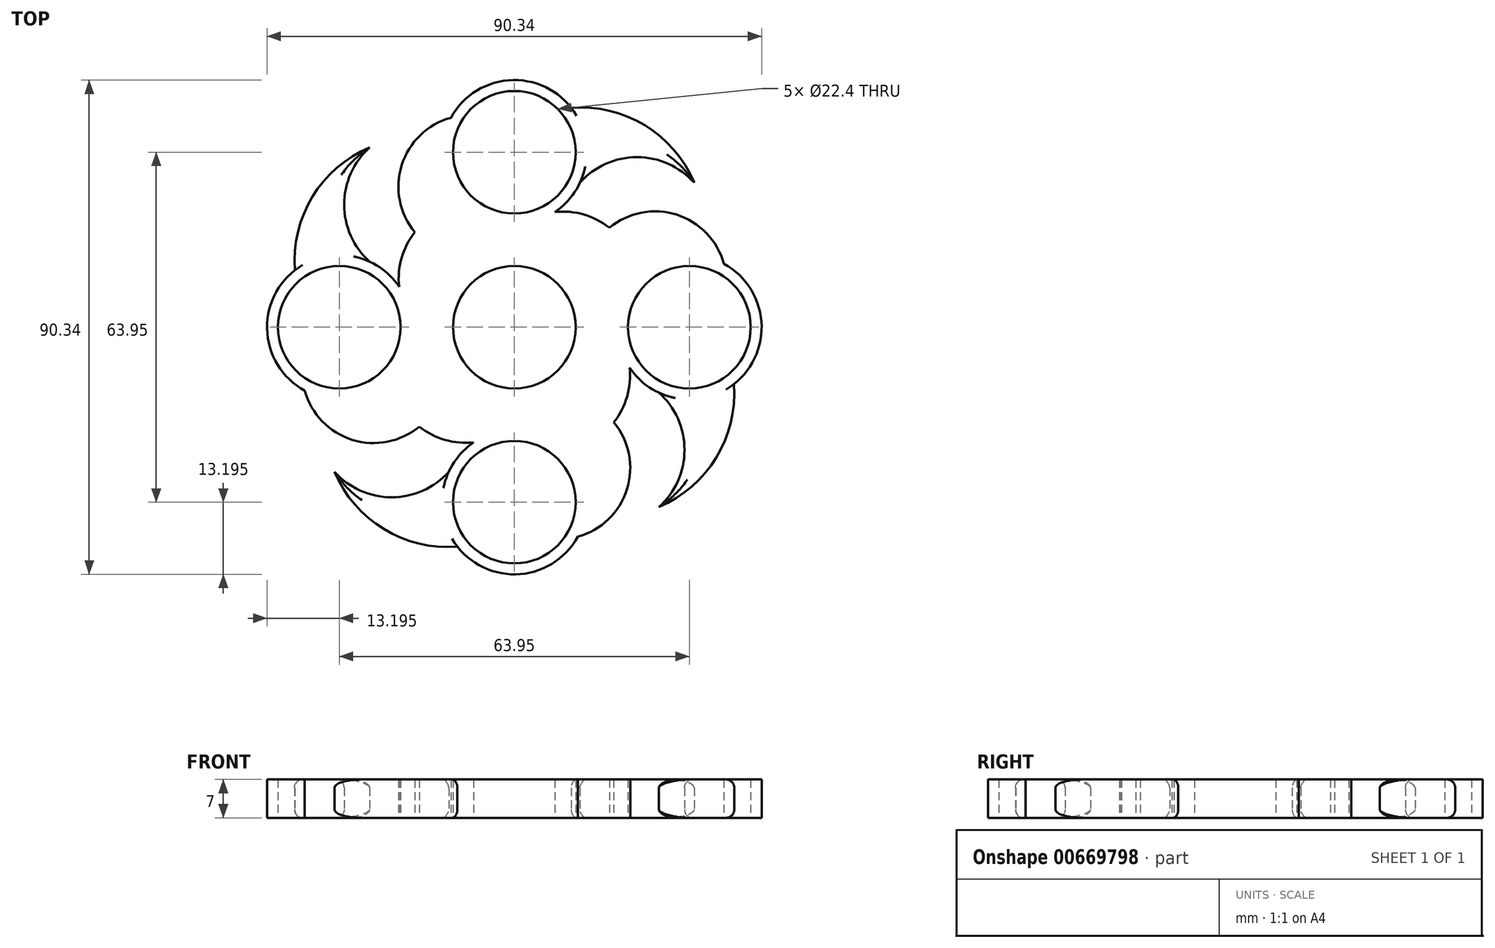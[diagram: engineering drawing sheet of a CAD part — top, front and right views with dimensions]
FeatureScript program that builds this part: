
annotation { "Feature Type Name" : "Feature", "Feature Type Description" : "" }
export const myFeature = defineFeature(function(context is Context, id is Id, definition is map)
    precondition{}
    {
        {
            var Q0;
            Q0=qCreatedBy(makeId("Top.planeOp"),FACE);
            var sketch = newSketch(context, id + "F0", { "sketchPlane" : qUnion([Q0])});
            skCircle(sketch, "E0", {"center": v(0, 0) * mm, "radius": 11.2 * mm});
            skCircle(sketch, "E1", {"center": v(0, 0) * mm, "radius": 13.2 * mm});
            skCircle(sketch, "E2", {"center": v(0, 31.97) * mm, "radius": 11.2 * mm});
            skCircle(sketch, "E3", {"center": v(0, 31.97) * mm, "radius": 13.2 * mm});
            skCircle(sketch, "E4.1.0", {"center": v(-31.97, 0) * mm, "radius": 13.2 * mm});
            skCircle(sketch, "E4.1.1", {"center": v(-31.97, 0) * mm, "radius": 11.2 * mm});
            skCircle(sketch, "E4.2.0", {"center": v(0, -31.97) * mm, "radius": 13.2 * mm});
            skCircle(sketch, "E4.2.1", {"center": v(0, -31.97) * mm, "radius": 11.2 * mm});
            skCircle(sketch, "E4.3.0", {"center": v(31.97, 0) * mm, "radius": 13.2 * mm});
            skCircle(sketch, "E4.3.1", {"center": v(31.97, 0) * mm, "radius": 11.2 * mm});
            skArc(sketch, "E5", {"start": v(-9.12, 22.43) * mm, "mid": v(-18.17, 17.37) * mm, "end": v(-21.05, 7.41) * mm});
            skArc(sketch, "E6.1.0", {"start": v(-22.43, -9.12) * mm, "mid": v(-17.37, -18.17) * mm, "end": v(-7.41, -21.05) * mm});
            skArc(sketch, "E6.2.0", {"start": v(9.12, -22.43) * mm, "mid": v(18.17, -17.37) * mm, "end": v(21.05, -7.41) * mm});
            skArc(sketch, "E6.3.0", {"start": v(22.43, 9.12) * mm, "mid": v(17.37, 18.17) * mm, "end": v(7.41, 21.05) * mm});
            skArc(sketch, "E7", {"start": v(32.85, 26.43) * mm, "mid": v(23.83, 36.9) * mm, "end": v(10.4, 40.1) * mm});
            skArc(sketch, "E8", {"start": v(32.85, 26.43) * mm, "mid": v(22.41, 31.09) * mm, "end": v(11.98, 26.43) * mm});
            skArc(sketch, "E9.1.0", {"start": v(-26.43, 32.85) * mm, "mid": v(-36.9, 23.83) * mm, "end": v(-40.1, 10.4) * mm});
            skArc(sketch, "E9.1.1", {"start": v(-26.43, 32.85) * mm, "mid": v(-31.09, 22.41) * mm, "end": v(-26.43, 11.98) * mm});
            skArc(sketch, "E9.2.0", {"start": v(-32.85, -26.43) * mm, "mid": v(-23.83, -36.9) * mm, "end": v(-10.4, -40.1) * mm});
            skArc(sketch, "E9.2.1", {"start": v(-32.85, -26.43) * mm, "mid": v(-22.41, -31.09) * mm, "end": v(-11.98, -26.43) * mm});
            skArc(sketch, "E9.3.0", {"start": v(26.43, -32.85) * mm, "mid": v(36.9, -23.83) * mm, "end": v(40.1, -10.4) * mm});
            skArc(sketch, "E9.3.1", {"start": v(26.43, -32.85) * mm, "mid": v(31.09, -22.41) * mm, "end": v(26.43, -11.98) * mm});
            skArc(sketch, "E10", {"start": v(-11.6, 38.29) * mm, "mid": v(-20.58, 29.62) * mm, "end": v(-18.17, 17.37) * mm});
            skArc(sketch, "E11.1.0", {"start": v(-38.29, -11.6) * mm, "mid": v(-29.62, -20.58) * mm, "end": v(-17.37, -18.17) * mm});
            skArc(sketch, "E11.2.0", {"start": v(11.6, -38.29) * mm, "mid": v(20.58, -29.62) * mm, "end": v(18.17, -17.37) * mm});
            skArc(sketch, "E11.3.0", {"start": v(38.29, 11.6) * mm, "mid": v(29.62, 20.58) * mm, "end": v(17.37, 18.17) * mm});
            skSolve(sketch);
        }
        {
            var Q0;
            Q0=makeQuery(id+"F0.imprint","IMPRINT",FACE,{"disambiguationData":[TD([[makeQuery(id+"F0.imprint","IMPRINT",EDGE,{"derivedFrom":sQuery(id+"F0.wireOp",EDGE,"E1")}),-1.0]])]});
            var Q1;
            Q1=makeQuery(id+"F0.imprint","IMPRINT",FACE,{"disambiguationData":[TD([[makeQuery(id+"F0.imprint","IMPRINT",EDGE,{"derivedFrom":sQuery(id+"F0.wireOp",EDGE,"E0")}),-1.0]])]});
            var Q2;
            Q2=makeQuery(id+"F0.imprint","IMPRINT",FACE,{"disambiguationData":[TD([[makeQuery(id+"F0.imprint","IMPRINT",EDGE,{"derivedFrom":sQuery(id+"F0.wireOp",EDGE,"E2")}),-1.0]])]});
            var Q3;
            {var subQ0=sQuery(id+"F0.wireOp",EDGE,"E7");Q3=makeQuery(id+"F0.imprint","IMPRINT",FACE,{"disambiguationData":[TD([[makeQuery(id+"F0.imprint","IMPRINT",EDGE,{"derivedFrom":subQ0}),1.0]])]});}
            var Q4;
            {var subQ3=sQuery(id+"F0.wireOp",EDGE,"E10");Q4=makeQuery(id+"F0.imprint","IMPRINT",FACE,{"disambiguationData":[TD([[makeQuery(id+"F0.imprint","IMPRINT",EDGE,{"derivedFrom":subQ3}),1.0]])]});}
            var Q5;
            Q5=makeQuery(id+"F0.imprint","IMPRINT",FACE,{"disambiguationData":[TD([[makeQuery(id+"F0.imprint","IMPRINT",EDGE,{"derivedFrom":sQuery(id+"F0.wireOp",EDGE,"E4.3.1")}),-1.0]])]});
            var Q6;
            {var subQ3=sQuery(id+"F0.wireOp",EDGE,"E11.3.0");Q6=makeQuery(id+"F0.imprint","IMPRINT",FACE,{"disambiguationData":[TD([[makeQuery(id+"F0.imprint","IMPRINT",EDGE,{"derivedFrom":subQ3}),1.0]])]});}
            var Q7;
            {var subQ0=sQuery(id+"F0.wireOp",EDGE,"E9.3.0");Q7=makeQuery(id+"F0.imprint","IMPRINT",FACE,{"disambiguationData":[TD([[makeQuery(id+"F0.imprint","IMPRINT",EDGE,{"derivedFrom":subQ0}),1.0]])]});}
            var Q8;
            {var subQ3=sQuery(id+"F0.wireOp",EDGE,"E11.2.0");Q8=makeQuery(id+"F0.imprint","IMPRINT",FACE,{"disambiguationData":[TD([[makeQuery(id+"F0.imprint","IMPRINT",EDGE,{"derivedFrom":subQ3}),1.0]])]});}
            var Q9;
            Q9=makeQuery(id+"F0.imprint","IMPRINT",FACE,{"disambiguationData":[TD([[makeQuery(id+"F0.imprint","IMPRINT",EDGE,{"derivedFrom":sQuery(id+"F0.wireOp",EDGE,"E4.2.1")}),-1.0]])]});
            var Q10;
            {var subQ0=sQuery(id+"F0.wireOp",EDGE,"E9.2.0");Q10=makeQuery(id+"F0.imprint","IMPRINT",FACE,{"disambiguationData":[TD([[makeQuery(id+"F0.imprint","IMPRINT",EDGE,{"derivedFrom":subQ0}),1.0]])]});}
            var Q11;
            {var subQ3=sQuery(id+"F0.wireOp",EDGE,"E11.1.0");Q11=makeQuery(id+"F0.imprint","IMPRINT",FACE,{"disambiguationData":[TD([[makeQuery(id+"F0.imprint","IMPRINT",EDGE,{"derivedFrom":subQ3}),1.0]])]});}
            var Q12;
            Q12=makeQuery(id+"F0.imprint","IMPRINT",FACE,{"disambiguationData":[TD([[makeQuery(id+"F0.imprint","IMPRINT",EDGE,{"derivedFrom":sQuery(id+"F0.wireOp",EDGE,"E4.1.1")}),-1.0]])]});
            var Q13;
            {var subQ0=sQuery(id+"F0.wireOp",EDGE,"E9.1.0");Q13=makeQuery(id+"F0.imprint","IMPRINT",FACE,{"disambiguationData":[TD([[makeQuery(id+"F0.imprint","IMPRINT",EDGE,{"derivedFrom":subQ0}),1.0]])]});}
            extrude(context, id + "F1", {"entities" : qUnion([Q0, Q1, Q2, Q3, Q4, Q5, Q6, Q7, Q8, Q9, Q10, Q11, Q12, Q13]), "depth" : 7 * mm, "offsetDistance" : 25 * mm});
        }
        {
            var Q0;
            Q0=makeQuery(id+"F1.opExtrude","CAP_EDGE",EDGE,{"disambiguationData":[OSD([sQuery(id+"F0.wireOp",EDGE,"E9.1.0")])],"isStart":false});
            var Q1;
            Q1=makeQuery(id+"F1.opExtrude","CAP_EDGE",EDGE,{"disambiguationData":[OSD([sQuery(id+"F0.wireOp",EDGE,"E7")])],"isStart":false});
            var Q2;
            Q2=makeQuery(id+"F1.opExtrude","CAP_EDGE",EDGE,{"disambiguationData":[OSD([sQuery(id+"F0.wireOp",EDGE,"E9.3.0")])],"isStart":false});
            var Q3;
            Q3=makeQuery(id+"F1.opExtrude","CAP_EDGE",EDGE,{"disambiguationData":[OSD([sQuery(id+"F0.wireOp",EDGE,"E9.2.0")])],"isStart":false});
            var Q4;
            Q4=makeQuery(id+"F1.opExtrude","CAP_EDGE",EDGE,{"disambiguationData":[OSD([sQuery(id+"F0.wireOp",EDGE,"E9.3.1")])],"isStart":false});
            var Q5;
            Q5=makeQuery(id+"F1.opExtrude","CAP_EDGE",EDGE,{"disambiguationData":[OSD([sQuery(id+"F0.wireOp",EDGE,"E9.2.1")])],"isStart":false});
            var Q6;
            Q6=makeQuery(id+"F1.opExtrude","CAP_EDGE",EDGE,{"disambiguationData":[OSD([sQuery(id+"F0.wireOp",EDGE,"E8")])],"isStart":false});
            var Q7;
            Q7=makeQuery(id+"F1.opExtrude","CAP_EDGE",EDGE,{"disambiguationData":[OSD([sQuery(id+"F0.wireOp",EDGE,"E9.1.1")])],"isStart":false});
            var Q8;
            Q8=makeQuery(id+"F1.opExtrude","CAP_EDGE",EDGE,{"disambiguationData":[OSD([sQuery(id+"F0.wireOp",EDGE,"E9.3.0")])],"isStart":true});
            var Q9;
            Q9=makeQuery(id+"F1.opExtrude","CAP_EDGE",EDGE,{"disambiguationData":[OSD([sQuery(id+"F0.wireOp",EDGE,"E9.2.1")])],"isStart":true});
            var Q10;
            Q10=makeQuery(id+"F1.opExtrude","CAP_EDGE",EDGE,{"disambiguationData":[OSD([sQuery(id+"F0.wireOp",EDGE,"E9.2.0")])],"isStart":true});
            var Q11;
            Q11=makeQuery(id+"F1.opExtrude","CAP_EDGE",EDGE,{"disambiguationData":[OSD([sQuery(id+"F0.wireOp",EDGE,"E9.3.1")])],"isStart":true});
            var Q12;
            Q12=makeQuery(id+"F1.opExtrude","CAP_EDGE",EDGE,{"disambiguationData":[OSD([sQuery(id+"F0.wireOp",EDGE,"E7")])],"isStart":true});
            var Q13;
            Q13=makeQuery(id+"F1.opExtrude","CAP_EDGE",EDGE,{"disambiguationData":[OSD([sQuery(id+"F0.wireOp",EDGE,"E8")])],"isStart":true});
            var Q14;
            Q14=makeQuery(id+"F1.opExtrude","CAP_EDGE",EDGE,{"disambiguationData":[OSD([sQuery(id+"F0.wireOp",EDGE,"E9.1.1")])],"isStart":true});
            var Q15;
            Q15=makeQuery(id+"F1.opExtrude","CAP_EDGE",EDGE,{"disambiguationData":[OSD([sQuery(id+"F0.wireOp",EDGE,"E9.1.0")])],"isStart":true});
            fillet(context, id + "F2", {"entities" : qUnion([Q0, Q1, Q2, Q3, Q4, Q5, Q6, Q7, Q8, Q9, Q10, Q11, Q12, Q13, Q14, Q15]), "radius" : 1.5 * mm, "tangentPropagation" : true, "allowEdgeOverflow" : false});
        }
    });
